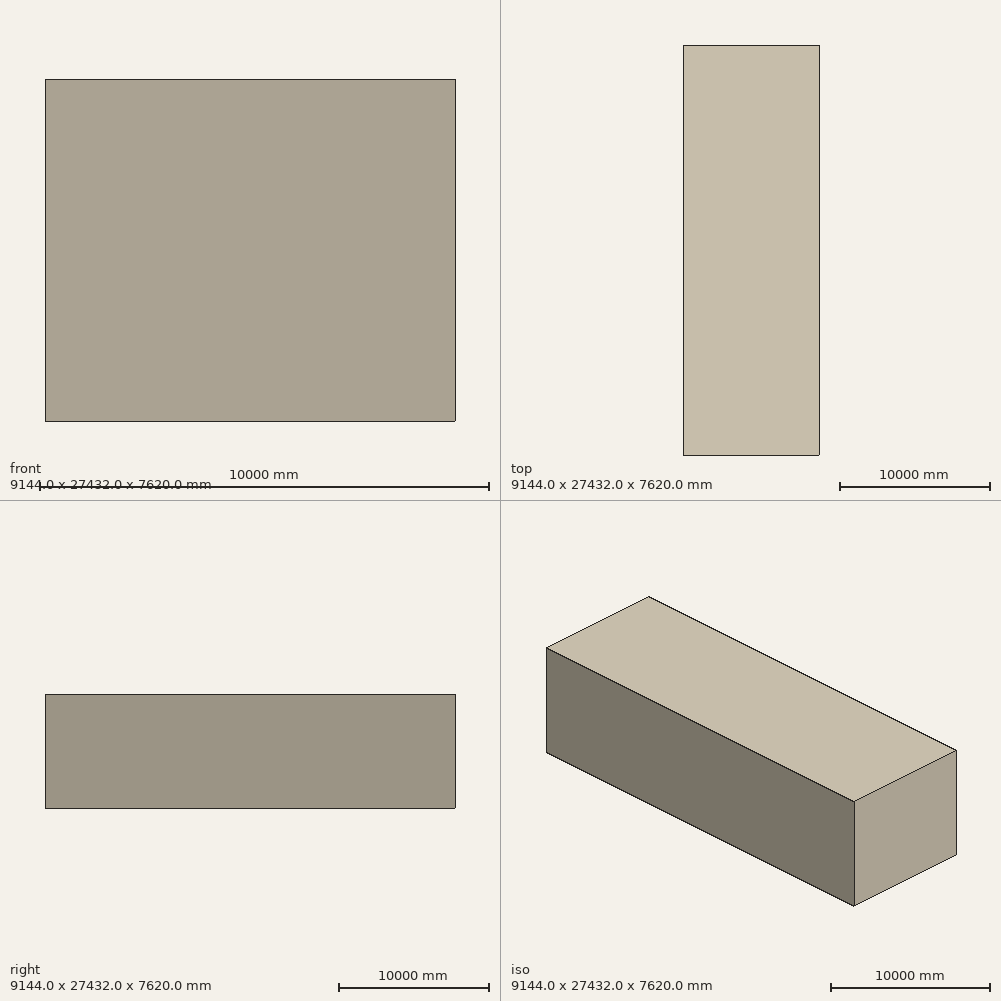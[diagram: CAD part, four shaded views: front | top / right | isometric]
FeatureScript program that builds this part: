
annotation { "Feature Type Name" : "Feature", "Feature Type Description" : "" }
export const myFeature = defineFeature(function(context is Context, id is Id, definition is map)
    precondition{}
    {
        {
            var Q0;
            Q0=qCreatedBy(makeId("Top.planeOp"),FACE);
            var sketch = newSketch(context, id + "F0", { "sketchPlane" : qUnion([Q0])});
            skLineSegment(sketch, "E0.bottom", {"start": v(-9144, 27432) * mm, "end": v(0, 27432) * mm});
            skLineSegment(sketch, "E0.top", {"start": v(-9144, 0) * mm, "end": v(0, 0) * mm});
            skLineSegment(sketch, "E0.left", {"start": v(-9144, 27432) * mm, "end": v(-9144, 0) * mm});
            skLineSegment(sketch, "E0.right", {"start": v(0, 27432) * mm, "end": v(0, 0) * mm});
            skSolve(sketch);
        }
        {
            var Q0;
            Q0 = qSketchRegion(id + "F0", true);
            extrude(context, id + "F1", {"entities" : qUnion([Q0]), "depth" : 7620 * mm});
        }
    });
